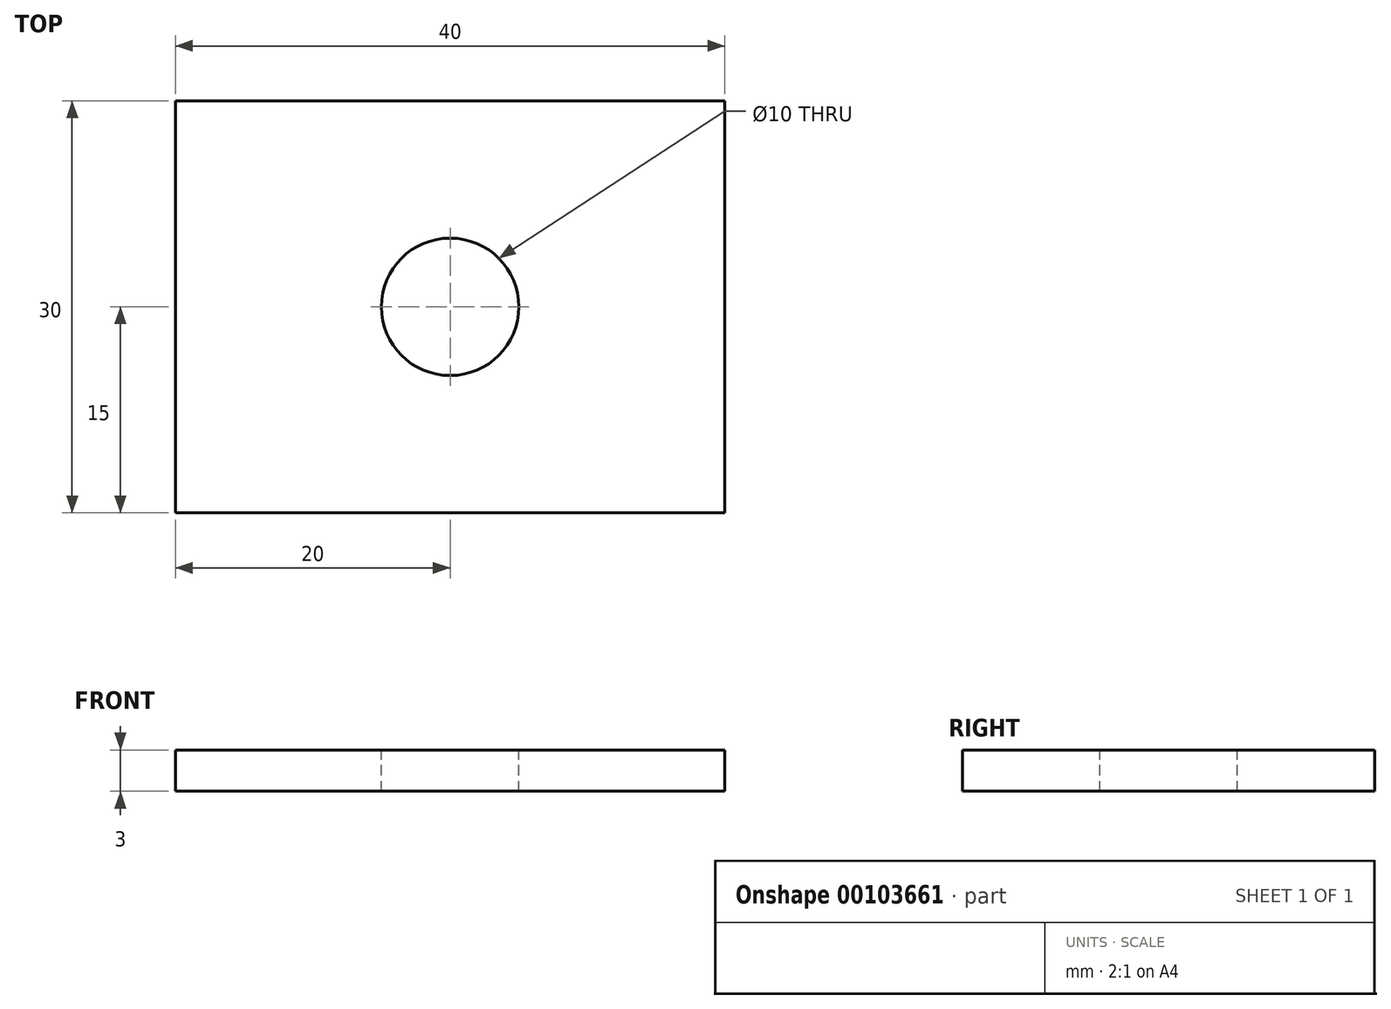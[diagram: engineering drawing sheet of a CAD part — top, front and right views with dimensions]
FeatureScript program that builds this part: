
annotation { "Feature Type Name" : "Feature", "Feature Type Description" : "" }
export const myFeature = defineFeature(function(context is Context, id is Id, definition is map)
    precondition{}
    {
        {
            var Q0;
            Q0=qCreatedBy(makeId("Top.planeOp"),FACE);
            var sketch = newSketch(context, id + "F0", { "sketchPlane" : qUnion([Q0])});
            skLineSegment(sketch, "E0.bottom", {"start": v(20, 15) * mm, "end": v(-20, 15) * mm});
            skLineSegment(sketch, "E0.top", {"start": v(20, -15) * mm, "end": v(-20, -15) * mm});
            skLineSegment(sketch, "E0.left", {"start": v(20, 15) * mm, "end": v(20, -15) * mm});
            skLineSegment(sketch, "E0.right", {"start": v(-20, 15) * mm, "end": v(-20, -15) * mm});
            skPoint(sketch, "E0.middle", {"position": v(0, 0) * mm});
            skSolve(sketch);
        }
        {
            var Q0;
            Q0 = qSketchRegion(id + "F0", true);
            extrude(context, id + "F1", {"entities" : qUnion([Q0]), "depth" : 3 * mm});
        }
        {
            var Q0;
            Q0=makeQuery(id+"F1.opExtrude","CAP_FACE",FACE,{"disambiguationData":[OSD([sQuery(id+"F0.wireOp",EDGE,"E0.bottom"),sQuery(id+"F0.wireOp",EDGE,"E0.top"),sQuery(id+"F0.wireOp",EDGE,"E0.left"),sQuery(id+"F0.wireOp",EDGE,"E0.right")])],"isStart":false});
            var sketch = newSketch(context, id + "F2", { "sketchPlane" : qUnion([Q0])});
            skCircle(sketch, "E1", {"center": v(0, 0) * mm, "radius": 5 * mm});
            skSolve(sketch);
        }
        {
            var Q0;
            Q0 = qSketchRegion(id + "F2", true);
            var Q1;
            Q1=makeQuery(id+"F1.opExtrude","CAP_FACE",FACE,{"disambiguationData":[OSD([sQuery(id+"F0.wireOp",EDGE,"E0.bottom"),sQuery(id+"F0.wireOp",EDGE,"E0.top"),sQuery(id+"F0.wireOp",EDGE,"E0.left"),sQuery(id+"F0.wireOp",EDGE,"E0.right")])],"isStart":true});
            extrude(context, id + "F3", {"entities" : qUnion([Q0]), "operationType" : NewBodyOperationType.REMOVE, "endBound" : BoundingType.UP_TO_SURFACE, "oppositeDirection" : true, "endBoundEntityFace" : qUnion([Q1]), "depth" : 25 * mm});
        }
    });
